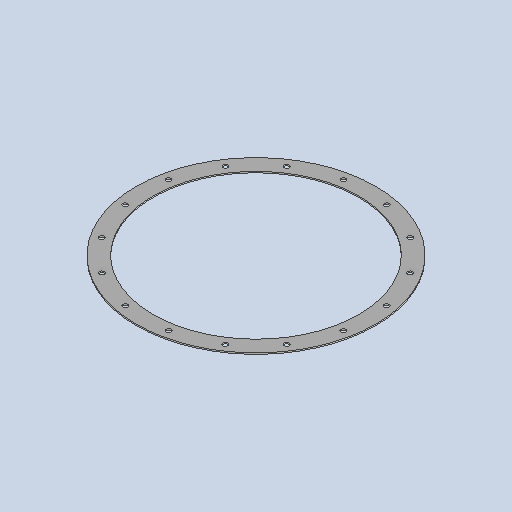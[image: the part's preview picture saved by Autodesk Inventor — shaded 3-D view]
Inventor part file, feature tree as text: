
AUTODESK INVENTOR PART (.ipt)
format: ipt  version: 2025 (Build 290162010, 162A)  size: 174,080 bytes
history: native  units: mm
features: sketch x3, extrude x2, other x2, sheet_metal_op x1, pattern_circular x1, projected_geometry x1
ambient origin geometry x8: Origin, YZ Plane, XZ Plane, XY Plane, X Axis, Y Axis, Z Axis, Center Point
bodies: Solid1 (feature_tree)
feature tree (10):
  sheet_metal_op  "Face1"
  extrude  "Extrusion1"  TaperAngle=0.0deg  [1 undecoded]
  extrude  "Extrusion2"  Depth=40.0mm
  pattern_circular  "Circular Pattern2"  [2 undecoded]
  sketch  "Sketch1"  dims[d2=3.0mm d4=0.0mm d5=0.0mm]
  other  "Plate1"
  sketch  "Sketch2"  dims[d9=530.0mm d11=40.0mm]
  projected_geometry  "Projected Loop1"
  sketch  "Sketch3"  dims[d20=1.963495mm d21=12.0mm d23=5.0mm d24=10.0mm d25=0.0mm d26=0.0mm d27=160.0mm d28=360.0deg]
  other  "Definition1"
note: 3 required parameter values undecoded (feature->parameter linkage not recoverable at this tier; creation-order binding heuristic only, values carry confidence <= 0.55)
